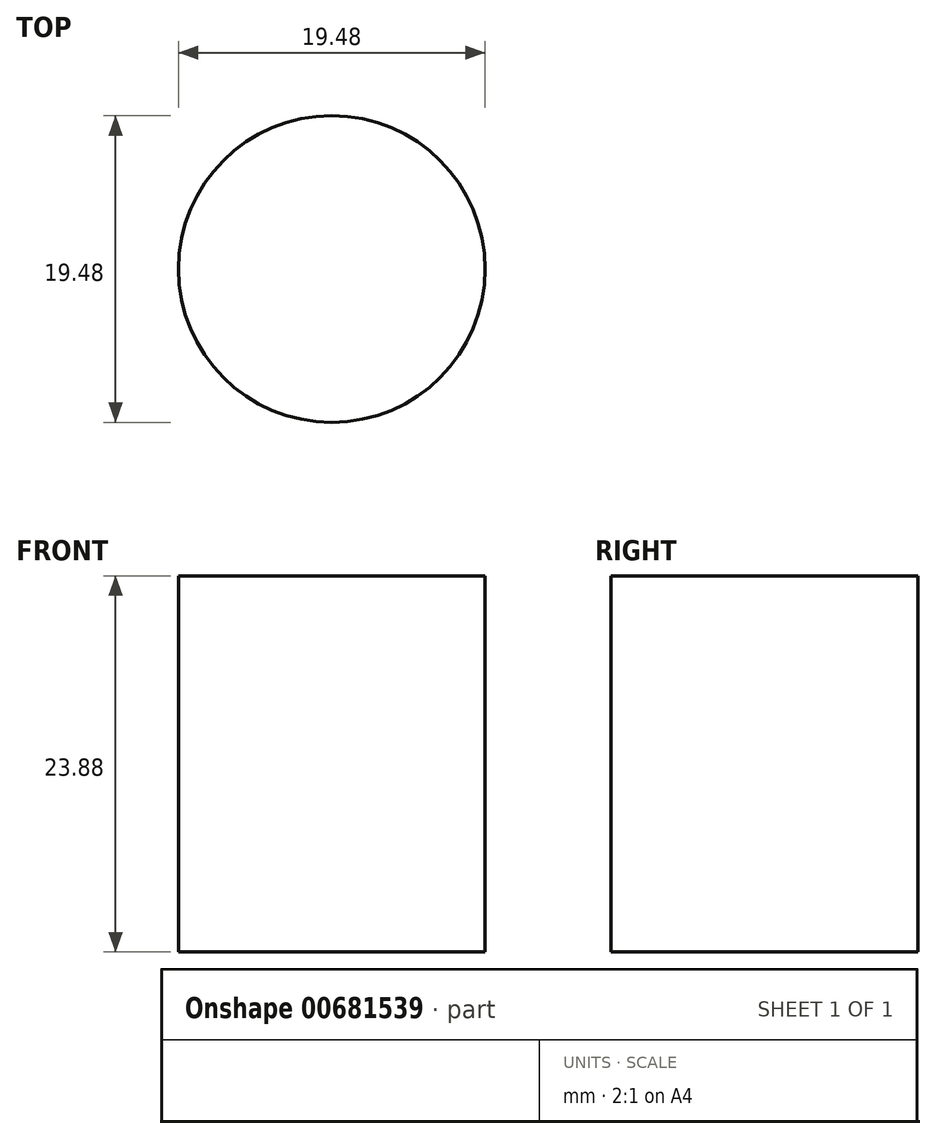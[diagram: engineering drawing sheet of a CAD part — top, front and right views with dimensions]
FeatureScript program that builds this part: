
annotation { "Feature Type Name" : "Feature", "Feature Type Description" : "" }
export const myFeature = defineFeature(function(context is Context, id is Id, definition is map)
    precondition{}
    {
        {
            var Q0;
            Q0=qCreatedBy(makeId("Top.planeOp"),FACE);
            var sketch = newSketch(context, id + "F0", { "sketchPlane" : qUnion([Q0])});
            skCircle(sketch, "E0", {"center": v(0, 0) * mm, "radius": 9.74 * mm});
            skSolve(sketch);
        }
        {
            var Q0;
            Q0 = qSketchRegion(id + "F0", true);
            extrude(context, id + "F1", {"entities" : qUnion([Q0]), "depth" : 23.88 * mm, "offsetDistance" : 25.4 * mm});
        }
    });
